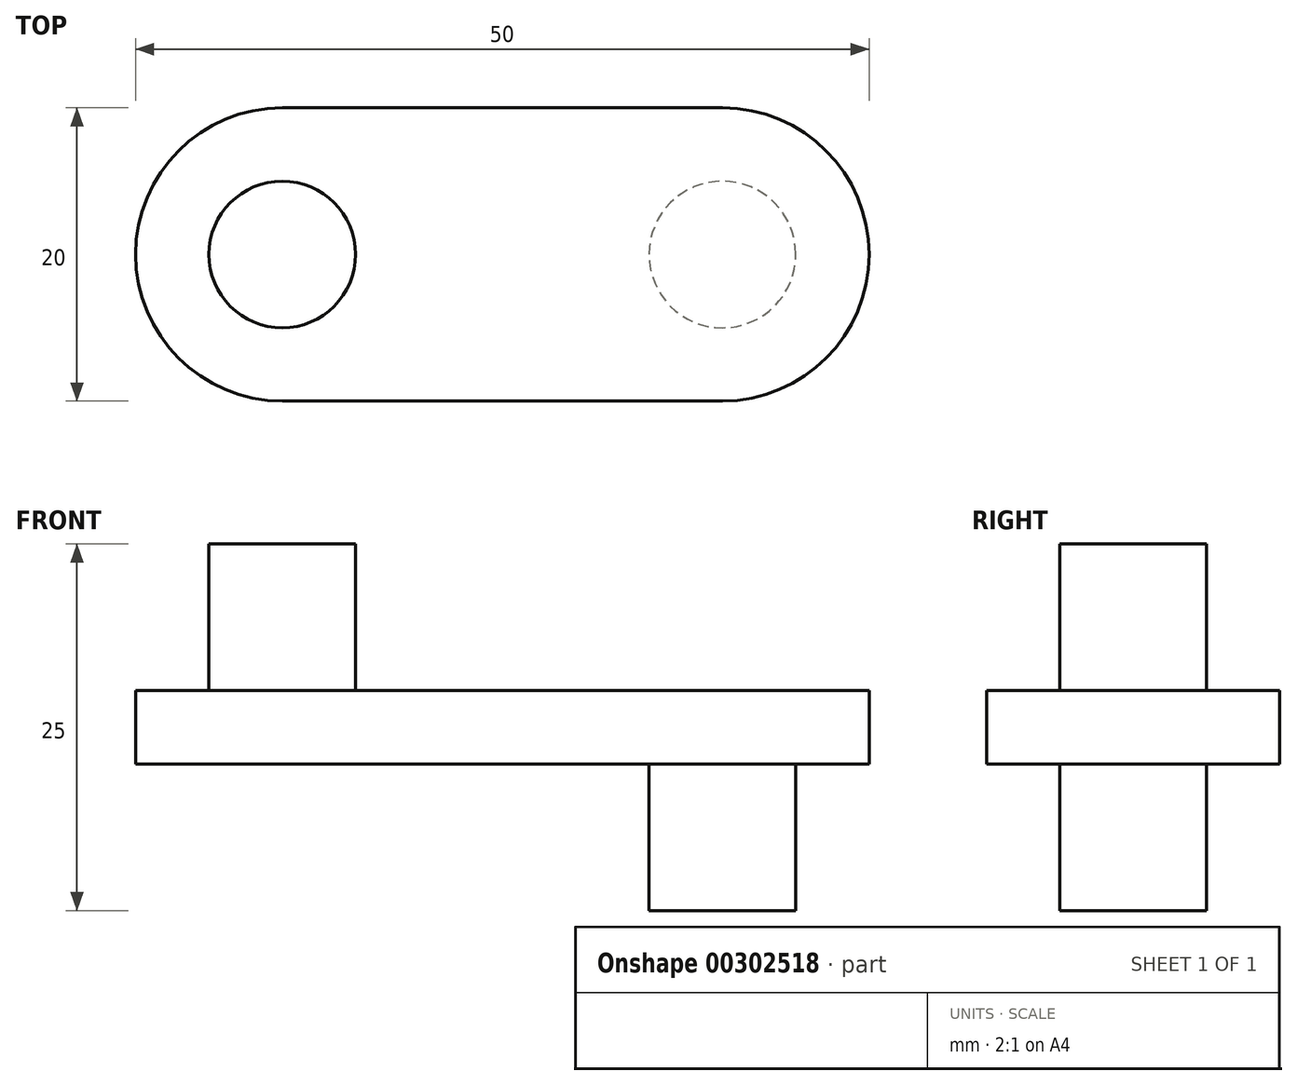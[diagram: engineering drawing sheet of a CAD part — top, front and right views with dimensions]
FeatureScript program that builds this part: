
annotation { "Feature Type Name" : "Feature", "Feature Type Description" : "" }
export const myFeature = defineFeature(function(context is Context, id is Id, definition is map)
    precondition{}
    {
        {
            var Q0;
            Q0=qCreatedBy(makeId("Top.planeOp"),FACE);
            var sketch = newSketch(context, id + "F0", { "sketchPlane" : qUnion([Q0])});
            skLineSegment(sketch, "E0", {"start": v(0, 0) * mm, "end": v(30, 0) * mm, "construction": true});
            skArc(sketch, "E1.0.startCap", {"start": v(0, -10) * mm, "mid": v(-10, 0) * mm, "end": v(0, 10) * mm});
            skArc(sketch, "E1.0.endCap", {"start": v(30, 10) * mm, "mid": v(40, 0) * mm, "end": v(30, -10) * mm});
            skLineSegment(sketch, "E1.0.left", {"start": v(0, 10) * mm, "end": v(30, 10) * mm});
            skLineSegment(sketch, "E1.0.right", {"start": v(0, -10) * mm, "end": v(30, -10) * mm});
            skSolve(sketch);
        }
        {
            var Q0;
            Q0 = qSketchRegion(id + "F0", true);
            extrude(context, id + "F1", {"entities" : qUnion([Q0]), "depth" : 5 * mm});
        }
        {
            var Q0;
            Q0=makeQuery(id+"F1.opExtrude","CAP_FACE",FACE,{"disambiguationData":[OSD([sQuery(id+"F0.wireOp",EDGE,"E1.0.startCap"),sQuery(id+"F0.wireOp",EDGE,"E1.0.endCap"),sQuery(id+"F0.wireOp",EDGE,"E1.0.left"),sQuery(id+"F0.wireOp",EDGE,"E1.0.right")])],"isStart":false});
            var sketch = newSketch(context, id + "F2", { "sketchPlane" : qUnion([Q0])});
            skCircle(sketch, "E2", {"center": v(0, 0) * mm, "radius": 5 * mm});
            skSolve(sketch);
        }
        {
            var Q0;
            Q0 = qSketchRegion(id + "F2", true);
            extrude(context, id + "F3", {"entities" : qUnion([Q0]), "operationType" : NewBodyOperationType.ADD, "depth" : 10 * mm});
        }
        {
            var Q0;
            Q0=makeQuery(id+"F1.opExtrude","CAP_FACE",FACE,{"disambiguationData":[OSD([sQuery(id+"F0.wireOp",EDGE,"E1.0.startCap"),sQuery(id+"F0.wireOp",EDGE,"E1.0.endCap"),sQuery(id+"F0.wireOp",EDGE,"E1.0.left"),sQuery(id+"F0.wireOp",EDGE,"E1.0.right")])],"isStart":true});
            var sketch = newSketch(context, id + "F4", { "sketchPlane" : qUnion([Q0])});
            skCircle(sketch, "E3", {"center": v(30, 0) * mm, "radius": 5 * mm});
            skSolve(sketch);
        }
        {
            var Q0;
            Q0 = qSketchRegion(id + "F4", true);
            extrude(context, id + "F5", {"entities" : qUnion([Q0]), "operationType" : NewBodyOperationType.ADD, "depth" : 10 * mm});
        }
    });
